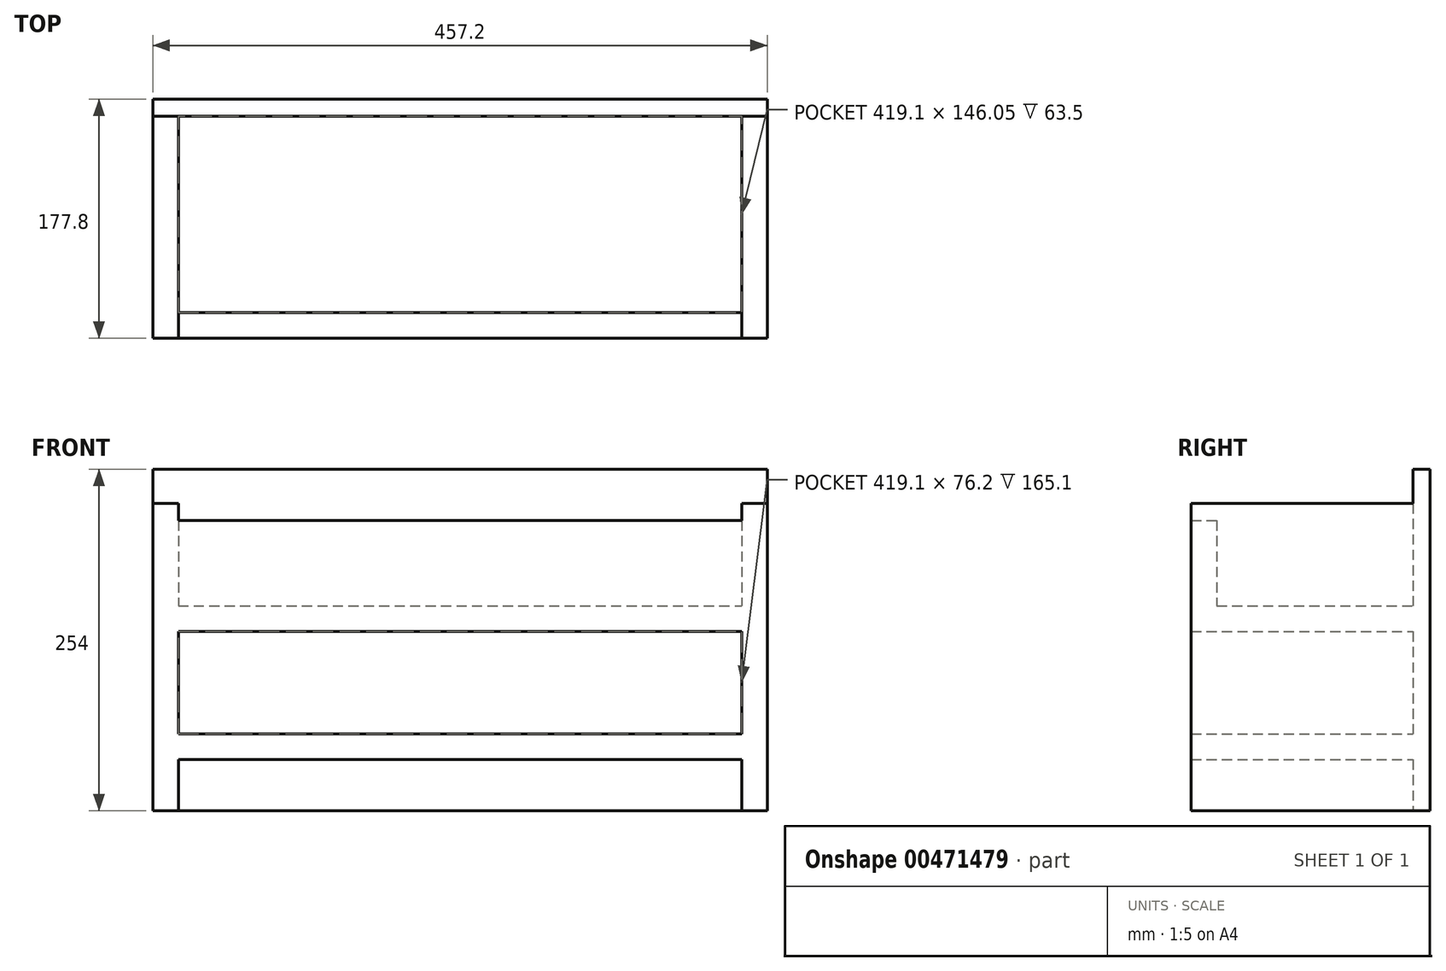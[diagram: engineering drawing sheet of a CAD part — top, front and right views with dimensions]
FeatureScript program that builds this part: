
annotation { "Feature Type Name" : "Feature", "Feature Type Description" : "" }
export const myFeature = defineFeature(function(context is Context, id is Id, definition is map)
    precondition{}
    {
        {
            var Q0;
            Q0=qCreatedBy(makeId("Front.planeOp"),FACE);
            var sketch = newSketch(context, id + "F0", { "sketchPlane" : qUnion([Q0])});
            skLineSegment(sketch, "E0.bottom", {"start": v(-228.6, 127) * mm, "end": v(228.6, 127) * mm});
            skLineSegment(sketch, "E0.top", {"start": v(-228.6, -127) * mm, "end": v(228.6, -127) * mm});
            skLineSegment(sketch, "E0.left", {"start": v(-228.6, 127) * mm, "end": v(-228.6, -127) * mm});
            skLineSegment(sketch, "E0.right", {"start": v(228.6, 127) * mm, "end": v(228.6, -127) * mm});
            skPoint(sketch, "E0.middle", {"position": v(0, 0) * mm});
            skSolve(sketch);
        }
        {
            var Q0;
            Q0=makeQuery(id+"F0.imprint","IMPRINT",FACE,{"disambiguationData":[TD([[makeQuery(id+"F0.imprint","IMPRINT",EDGE,{"derivedFrom":sQuery(id+"F0.wireOp",EDGE,"E0.bottom")}),-1.0]])]});
            extrude(context, id + "F1", {"entities" : qUnion([Q0]), "depth" : 12.7 * mm});
        }
        {
            var Q0;
            Q0=makeQuery(id+"F1.opExtrude","CAP_FACE",FACE,{"disambiguationData":[OSD([sQuery(id+"F0.wireOp",EDGE,"E0.bottom"),sQuery(id+"F0.wireOp",EDGE,"E0.top"),sQuery(id+"F0.wireOp",EDGE,"E0.left"),sQuery(id+"F0.wireOp",EDGE,"E0.right")])],"isStart":false});
            var sketch = newSketch(context, id + "F2", { "sketchPlane" : qUnion([Q0])});
            skLineSegment(sketch, "E1.bottom", {"start": v(-228.6, 101.6) * mm, "end": v(-209.55, 101.6) * mm});
            skLineSegment(sketch, "E1.top", {"start": v(-228.6, -127) * mm, "end": v(-209.55, -127) * mm});
            skLineSegment(sketch, "E1.left", {"start": v(-228.6, 101.6) * mm, "end": v(-228.6, -127) * mm});
            skLineSegment(sketch, "E1.right", {"start": v(-209.55, 101.6) * mm, "end": v(-209.55, -127) * mm});
            skLineSegment(sketch, "E2.MirrorCS", {"start": v(228.6, -127) * mm, "end": v(209.55, -127) * mm});
            skLineSegment(sketch, "E3.MirrorCS", {"start": v(209.55, 101.6) * mm, "end": v(209.55, -127) * mm});
            skLineSegment(sketch, "E4.MirrorCS", {"start": v(228.6, 101.6) * mm, "end": v(209.55, 101.6) * mm});
            skLineSegment(sketch, "E5.MirrorCS", {"start": v(228.6, 101.6) * mm, "end": v(228.6, -127) * mm});
            skSolve(sketch);
        }
        {
            var Q0;
            Q0 = qSketchRegion(id + "F2", true);
            extrude(context, id + "F3", {"entities" : qUnion([Q0]), "operationType" : NewBodyOperationType.ADD, "depth" : 165.1 * mm});
        }
        {
            var Q0;
            Q0=makeQuery(id+"F3.opExtrude","SWEPT_FACE",FACE,{"disambiguationData":[OSD([sQuery(id+"F2.wireOp",EDGE,"E1.right")])]});
            var sketch = newSketch(context, id + "F4", { "sketchPlane" : qUnion([Q0])});
            skLineSegment(sketch, "E6.bottom", {"start": v(-177.8, 88.9) * mm, "end": v(-158.75, 88.9) * mm});
            skLineSegment(sketch, "E6.top", {"start": v(-177.8, 25.4) * mm, "end": v(-158.75, 25.4) * mm});
            skLineSegment(sketch, "E6.left", {"start": v(-177.8, 88.9) * mm, "end": v(-177.8, 25.4) * mm});
            skLineSegment(sketch, "E6.right", {"start": v(-158.75, 88.9) * mm, "end": v(-158.75, 25.4) * mm});
            skSolve(sketch);
        }
        {
            var Q0;
            Q0 = qSketchRegion(id + "F4", true);
            extrude(context, id + "F5", {"entities" : qUnion([Q0]), "operationType" : NewBodyOperationType.ADD, "endBound" : BoundingType.UP_TO_NEXT, "depth" : 25.4 * mm});
        }
        {
            var Q0;
            Q0=makeQuery(id+"F1.opExtrude","CAP_FACE",FACE,{"disambiguationData":[OSD([sQuery(id+"F0.wireOp",EDGE,"E0.bottom"),sQuery(id+"F0.wireOp",EDGE,"E0.top"),sQuery(id+"F0.wireOp",EDGE,"E0.left"),sQuery(id+"F0.wireOp",EDGE,"E0.right")])],"isStart":false});
            var sketch = newSketch(context, id + "F6", { "sketchPlane" : qUnion([Q0])});
            skLineSegment(sketch, "E7.bottom", {"start": v(-209.55, 25.4) * mm, "end": v(209.55, 25.4) * mm});
            skLineSegment(sketch, "E7.top", {"start": v(-209.55, 6.35) * mm, "end": v(209.55, 6.35) * mm});
            skLineSegment(sketch, "E7.left", {"start": v(-209.55, 6.35) * mm, "end": v(-209.55, 25.4) * mm});
            skLineSegment(sketch, "E7.right", {"start": v(209.55, 6.35) * mm, "end": v(209.55, 25.4) * mm});
            skSolve(sketch);
        }
        {
            var Q0;
            Q0 = qSketchRegion(id + "F6", true);
            var Q1;
            Q1=makeQuery(id+"F5.boolean.opBoolean","MERGE",FACE,{"derivedFrom":[makeQuery(id+"F3.opExtrude","CAP_FACE",FACE,{"disambiguationData":[OSD([sQuery(id+"F2.wireOp",EDGE,"E1.bottom"),sQuery(id+"F2.wireOp",EDGE,"E1.top"),sQuery(id+"F2.wireOp",EDGE,"E1.left"),sQuery(id+"F2.wireOp",EDGE,"E1.right")])],"isStart":false}),makeQuery(id+"F3.opExtrude","CAP_FACE",FACE,{"disambiguationData":[OSD([sQuery(id+"F2.wireOp",EDGE,"E2.MirrorCS"),sQuery(id+"F2.wireOp",EDGE,"E3.MirrorCS"),sQuery(id+"F2.wireOp",EDGE,"E4.MirrorCS"),sQuery(id+"F2.wireOp",EDGE,"E5.MirrorCS")])],"isStart":false}),makeQuery(id+"F5.opExtrude","SWEPT_FACE",FACE,{"disambiguationData":[OSD([sQuery(id+"F4.wireOp",EDGE,"E6.left")])]})]});
            extrude(context, id + "F7", {"entities" : qUnion([Q0]), "operationType" : NewBodyOperationType.ADD, "endBound" : BoundingType.UP_TO_SURFACE, "endBoundEntityFace" : qUnion([Q1]), "depth" : 25.4 * mm});
        }
        {
            var Q0;
            {var subQ1=sQuery(id+"F2.wireOp",EDGE,"E1.right");var subQ4=sQuery(id+"F0.wireOp",EDGE,"E0.top");Q0=makeQuery(id+"F7.boolean.opBoolean","SPLIT",FACE,{"disambiguationData":[TD([makeQuery(id+"F1.opExtrude","SWEPT_FACE",FACE,{"disambiguationData":[OSD([subQ4])]})])],"derivedFrom":makeQuery(id+"F3.opExtrude","SWEPT_FACE",FACE,{"disambiguationData":[OSD([subQ1])]})});}
            var sketch = newSketch(context, id + "F8", { "sketchPlane" : qUnion([Q0])});
            skLineSegment(sketch, "E8.bottom", {"start": v(-177.8, -88.9) * mm, "end": v(-12.7, -88.9) * mm});
            skLineSegment(sketch, "E8.top", {"start": v(-177.8, -69.85) * mm, "end": v(-12.7, -69.85) * mm});
            skLineSegment(sketch, "E8.left", {"start": v(-177.8, -88.9) * mm, "end": v(-177.8, -69.85) * mm});
            skLineSegment(sketch, "E8.right", {"start": v(-12.7, -88.9) * mm, "end": v(-12.7, -69.85) * mm});
            skSolve(sketch);
        }
        {
            var Q0;
            Q0 = qSketchRegion(id + "F8", true);
            extrude(context, id + "F9", {"entities" : qUnion([Q0]), "operationType" : NewBodyOperationType.ADD, "endBound" : BoundingType.UP_TO_NEXT, "depth" : 25.4 * mm});
        }
    });
